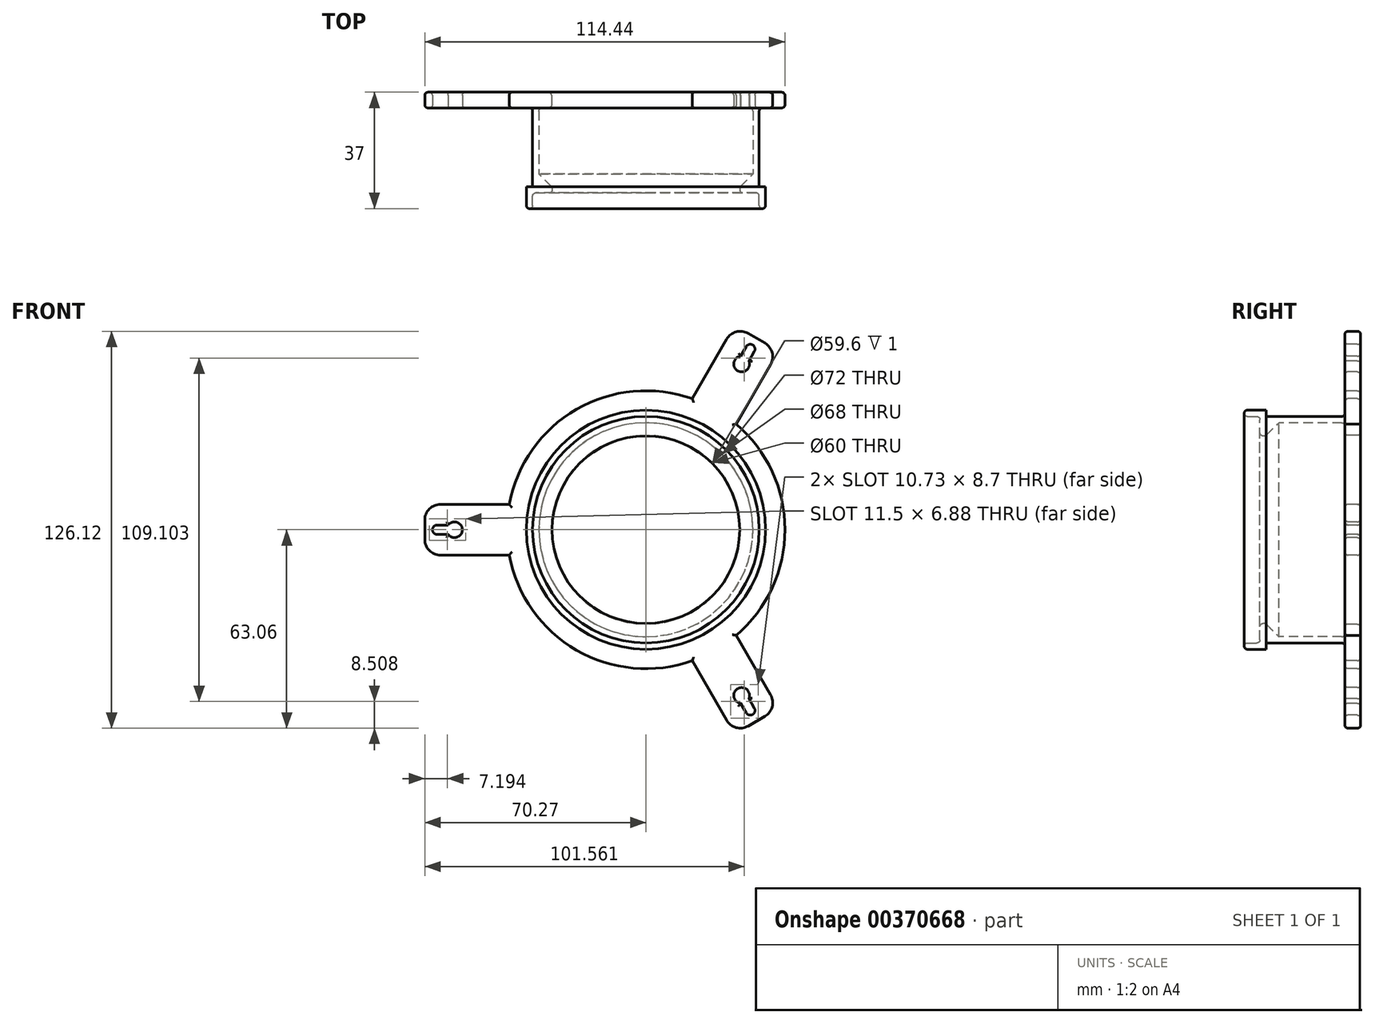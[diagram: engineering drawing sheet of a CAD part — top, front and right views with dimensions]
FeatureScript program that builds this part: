
annotation { "Feature Type Name" : "Feature", "Feature Type Description" : "" }
export const myFeature = defineFeature(function(context is Context, id is Id, definition is map)
    precondition{}
    {
        {
            var Q0;
            Q0=qCreatedBy(makeId("Front.planeOp"),FACE);
            var sketch = newSketch(context, id + "F0", { "sketchPlane" : qUnion([Q0])});
            skCircle(sketch, "E0", {"center": v(0, 0) * mm, "radius": 31.8 * mm});
            skCircle(sketch, "E1", {"center": v(0, 0) * mm, "radius": 36 * mm});
            skCircle(sketch, "E2", {"center": v(0, 0) * mm, "radius": 29.8 * mm});
            skCircle(sketch, "E3", {"center": v(0, 0) * mm, "radius": 38 * mm});
            skSolve(sketch);
        }
        {
            var Q0;
            Q0=makeQuery(id+"F0.imprint","IMPRINT",FACE,{"disambiguationData":[TD([[makeQuery(id+"F0.imprint","IMPRINT",EDGE,{"derivedFrom":sQuery(id+"F0.wireOp",EDGE,"E0")}),-1.0]])]});
            var Q1;
            Q1=makeQuery(id+"F0.imprint","IMPRINT",FACE,{"disambiguationData":[TD([[makeQuery(id+"F0.imprint","IMPRINT",EDGE,{"derivedFrom":sQuery(id+"F0.wireOp",EDGE,"E1")}),-1.0]])]});
            var Q2;
            Q2=makeQuery(id+"F0.imprint","IMPRINT",FACE,{"disambiguationData":[TD([[makeQuery(id+"F0.imprint","IMPRINT",EDGE,{"derivedFrom":sQuery(id+"F0.wireOp",EDGE,"E0")}),1.0]])]});
            extrude(context, id + "F1", {"entities" : qUnion([Q0, Q1, Q2]), "oppositeDirection" : true, "depth" : 2 * mm});
        }
        {
            var Q0;
            Q0=makeQuery(id+"F0.imprint","IMPRINT",FACE,{"disambiguationData":[TD([[makeQuery(id+"F0.imprint","IMPRINT",EDGE,{"derivedFrom":sQuery(id+"F0.wireOp",EDGE,"E1")}),-1.0]])]});
            extrude(context, id + "F2", {"entities" : qUnion([Q0]), "operationType" : NewBodyOperationType.ADD, "depth" : 5 * mm});
        }
        {
            var Q0;
            Q0=makeQuery(id+"F2.opExtrude","CAP_FACE",FACE,{"disambiguationData":[OSD([sQuery(id+"F0.wireOp",EDGE,"E1"),sQuery(id+"F0.wireOp",EDGE,"E3")])],"isStart":false});
            var Q1;
            Q1=makeQuery(id+"F2.opExtrude","CAP_FACE",FACE,{"disambiguationData":[OSD([sQuery(id+"F0.wireOp",EDGE,"E0"),sQuery(id+"F0.wireOp",EDGE,"E2")])],"isStart":false});
            var Q2;
            Q2=makeQuery(id+"F1.opExtrude","CAP_FACE",FACE,{"disambiguationData":[OSD([sQuery(id+"F0.wireOp",EDGE,"E2"),sQuery(id+"F0.wireOp",EDGE,"E3")])],"isStart":true});
            fillet(context, id + "F3", {"entities" : qUnion([Q0, Q1, Q2]), "radius" : 1 * mm, "tangentPropagation" : true, "allowEdgeOverflow" : false});
        }
        {
            var Q0;
            Q0=makeQuery(id+"F1.opExtrude","CAP_FACE",FACE,{"disambiguationData":[OSD([sQuery(id+"F0.wireOp",EDGE,"E2"),sQuery(id+"F0.wireOp",EDGE,"E3")])],"isStart":false});
            var sketch = newSketch(context, id + "F4", { "sketchPlane" : qUnion([Q0])});
            skCircle(sketch, "E4", {"center": v(0, 0) * mm, "radius": 34 * mm});
            skCircle(sketch, "E5", {"center": v(0, 0) * mm, "radius": 36 * mm});
            skSolve(sketch);
        }
        {
            var Q0;
            Q0 = qSketchRegion(id + "F4", true);
            extrude(context, id + "F5", {"entities" : qUnion([Q0]), "operationType" : NewBodyOperationType.ADD, "depth" : 25 * mm});
        }
        {
            var Q0;
            Q0=makeQuery(id+"F5.opExtrude","CAP_FACE",FACE,{"disambiguationData":[OSD([sQuery(id+"F4.wireOp",EDGE,"E4"),sQuery(id+"F4.wireOp",EDGE,"E5")])],"isStart":false});
            var sketch = newSketch(context, id + "F6", { "sketchPlane" : qUnion([Q0])});
            skCircle(sketch, "E6", {"center": v(0, 0) * mm, "radius": 30 * mm});
            skCircle(sketch, "E7", {"center": v(0, 0) * mm, "radius": 44.17 * mm});
            skLineSegment(sketch, "E8.bottom", {"start": v(35.08, 8.07) * mm, "end": v(65.27, 8.07) * mm});
            skLineSegment(sketch, "E8.top", {"start": v(35.08, -8.07) * mm, "end": v(65.27, -8.07) * mm});
            skLineSegment(sketch, "E8.left", {"start": v(35.08, 8.07) * mm, "end": v(35.08, -8.07) * mm});
            skLineSegment(sketch, "E8.right", {"start": v(70.27, 3.07) * mm, "end": v(70.27, -3.07) * mm});
            skCircle(sketch, "E9", {"center": v(60.83, 0) * mm, "radius": 2.5 * mm});
            skLineSegment(sketch, "E10.bottom", {"start": v(62.83, 1.5) * mm, "end": v(66.33, 1.5) * mm});
            skLineSegment(sketch, "E10.top", {"start": v(62.83, -1.5) * mm, "end": v(66.33, -1.5) * mm});
            skLineSegment(sketch, "E10.left", {"start": v(62.83, 1.5) * mm, "end": v(62.83, -1.5) * mm});
            skLineSegment(sketch, "E10.right", {"start": v(67.83, 0) * mm, "end": v(67.83, 0) * mm});
            skPoint(sketch, "E11.visualSharp", {"position": v(70.27, 8.07) * mm});
            skArc(sketch, "E11.filletArc", {"start": v(70.27, 3.07) * mm, "mid": v(68.8, 6.6) * mm, "end": v(65.27, 8.07) * mm});
            skPoint(sketch, "E12.visualSharp", {"position": v(70.27, -8.07) * mm});
            skArc(sketch, "E12.filletArc", {"start": v(65.27, -8.07) * mm, "mid": v(68.8, -6.6) * mm, "end": v(70.27, -3.07) * mm});
            skPoint(sketch, "E13.visualSharp", {"position": v(67.83, 1.5) * mm});
            skArc(sketch, "E13.filletArc", {"start": v(67.83, 0) * mm, "mid": v(67.39, 1.06) * mm, "end": v(66.33, 1.5) * mm});
            skPoint(sketch, "E14.visualSharp", {"position": v(67.83, -1.5) * mm});
            skArc(sketch, "E14.filletArc", {"start": v(66.33, -1.5) * mm, "mid": v(67.39, -1.06) * mm, "end": v(67.83, 0) * mm});
            skLineSegment(sketch, "E15.1.1", {"start": v(-24.53, 26.35) * mm, "end": v(-10.55, 34.42) * mm});
            skLineSegment(sketch, "E15.1.2", {"start": v(-10.55, 34.42) * mm, "end": v(-25.65, 60.56) * mm});
            skLineSegment(sketch, "E15.1.3", {"start": v(-24.53, 26.35) * mm, "end": v(-39.63, 52.5) * mm});
            skPoint(sketch, "E15.1.5", {"position": v(-42.13, 56.82) * mm});
            skPoint(sketch, "E15.1.6", {"position": v(-28.15, 64.9) * mm});
            skPoint(sketch, "E15.1.7", {"position": v(-32.61, 59.49) * mm});
            skCircle(sketch, "E15.1.8", {"center": v(-30.41, 52.68) * mm, "radius": 2.5 * mm});
            skArc(sketch, "E15.1.9", {"start": v(-37.8, 59.32) * mm, "mid": v(-40.13, 56.29) * mm, "end": v(-39.63, 52.5) * mm});
            skArc(sketch, "E15.1.10", {"start": v(-25.65, 60.56) * mm, "mid": v(-28.68, 62.9) * mm, "end": v(-32.48, 62.4) * mm});
            skPoint(sketch, "E15.1.11", {"position": v(-35.21, 57.99) * mm});
            skLineSegment(sketch, "E15.1.12", {"start": v(-37.8, 59.32) * mm, "end": v(-32.48, 62.4) * mm});
            skLineSegment(sketch, "E15.1.13", {"start": v(-32.71, 53.66) * mm, "end": v(-30.11, 55.16) * mm});
            skLineSegment(sketch, "E15.1.14", {"start": v(-32.71, 53.66) * mm, "end": v(-34.46, 56.7) * mm});
            skLineSegment(sketch, "E15.1.15", {"start": v(-30.11, 55.16) * mm, "end": v(-31.86, 58.2) * mm});
            skArc(sketch, "E15.1.16", {"start": v(-31.86, 58.2) * mm, "mid": v(-32.77, 58.89) * mm, "end": v(-33.91, 58.74) * mm});
            skArc(sketch, "E15.1.17", {"start": v(-33.91, 58.74) * mm, "mid": v(-34.61, 57.83) * mm, "end": v(-34.46, 56.7) * mm});
            skLineSegment(sketch, "E15.2.1", {"start": v(-10.55, -34.42) * mm, "end": v(-24.53, -26.35) * mm});
            skLineSegment(sketch, "E15.2.2", {"start": v(-24.53, -26.35) * mm, "end": v(-39.63, -52.5) * mm});
            skLineSegment(sketch, "E15.2.3", {"start": v(-10.55, -34.42) * mm, "end": v(-25.65, -60.56) * mm});
            skPoint(sketch, "E15.2.5", {"position": v(-28.15, -64.9) * mm});
            skPoint(sketch, "E15.2.6", {"position": v(-42.13, -56.82) * mm});
            skPoint(sketch, "E15.2.7", {"position": v(-35.21, -57.99) * mm});
            skCircle(sketch, "E15.2.8", {"center": v(-30.41, -52.68) * mm, "radius": 2.5 * mm});
            skArc(sketch, "E15.2.9", {"start": v(-32.48, -62.4) * mm, "mid": v(-28.68, -62.9) * mm, "end": v(-25.65, -60.56) * mm});
            skArc(sketch, "E15.2.10", {"start": v(-39.63, -52.5) * mm, "mid": v(-40.13, -56.29) * mm, "end": v(-37.8, -59.32) * mm});
            skPoint(sketch, "E15.2.11", {"position": v(-32.61, -59.49) * mm});
            skLineSegment(sketch, "E15.2.12", {"start": v(-32.48, -62.4) * mm, "end": v(-37.8, -59.32) * mm});
            skLineSegment(sketch, "E15.2.13", {"start": v(-30.11, -55.16) * mm, "end": v(-32.71, -53.66) * mm});
            skLineSegment(sketch, "E15.2.14", {"start": v(-30.11, -55.16) * mm, "end": v(-31.86, -58.2) * mm});
            skLineSegment(sketch, "E15.2.15", {"start": v(-32.71, -53.66) * mm, "end": v(-34.46, -56.7) * mm});
            skArc(sketch, "E15.2.16", {"start": v(-34.46, -56.7) * mm, "mid": v(-34.61, -57.83) * mm, "end": v(-33.91, -58.74) * mm});
            skArc(sketch, "E15.2.17", {"start": v(-33.91, -58.74) * mm, "mid": v(-32.77, -58.89) * mm, "end": v(-31.86, -58.2) * mm});
            skSolve(sketch);
        }
        {
            var Q0;
            Q0 = qSketchRegion(id + "F6", true);
            extrude(context, id + "F7", {"entities" : qUnion([Q0]), "operationType" : NewBodyOperationType.ADD, "depth" : 5 * mm});
        }
        {
            var Q0;
            Q0=makeQuery(id+"F5.opExtrude","CAP_EDGE",EDGE,{"disambiguationData":[OSD([sQuery(id+"F4.wireOp",EDGE,"E4")])],"isStart":true});
            var Q1;
            Q1=makeQuery(id+"F5.opExtrude","CAP_EDGE",EDGE,{"disambiguationData":[OSD([sQuery(id+"F4.wireOp",EDGE,"E5")])],"isStart":true});
            chamfer(context, id + "F8", {"entities" : qUnion([Q0, Q1]), "width" : 4 * mm, "tangentPropagation" : true});
        }
        {
            var Q0;
            Q0=makeQuery(id+"F7.opExtrude","CAP_FACE",FACE,{"disambiguationData":[OSD([sQuery(id+"F6.wireOp",EDGE,"E8.bottom"),sQuery(id+"F6.wireOp",EDGE,"E8.top"),sQuery(id+"F6.wireOp",EDGE,"E8.right"),sQuery(id+"F6.wireOp",EDGE,"E9"),sQuery(id+"F6.wireOp",EDGE,"E10.bottom"),sQuery(id+"F6.wireOp",EDGE,"E10.top"),sQuery(id+"F6.wireOp",EDGE,"E11.filletArc"),sQuery(id+"F6.wireOp",EDGE,"E12.filletArc"),sQuery(id+"F6.wireOp",EDGE,"E13.filletArc"),sQuery(id+"F6.wireOp",EDGE,"E14.filletArc"),sQuery(id+"F6.wireOp",EDGE,"E15.1.2"),sQuery(id+"F6.wireOp",EDGE,"E15.1.3"),sQuery(id+"F6.wireOp",EDGE,"E15.1.8"),sQuery(id+"F6.wireOp",EDGE,"E15.1.9"),sQuery(id+"F6.wireOp",EDGE,"E15.1.10"),sQuery(id+"F6.wireOp",EDGE,"E15.1.12"),sQuery(id+"F6.wireOp",EDGE,"E15.1.14"),sQuery(id+"F6.wireOp",EDGE,"E15.1.15"),sQuery(id+"F6.wireOp",EDGE,"E15.1.16"),sQuery(id+"F6.wireOp",EDGE,"E15.1.17"),sQuery(id+"F6.wireOp",EDGE,"E6"),sQuery(id+"F6.wireOp",EDGE,"E15.2.2"),sQuery(id+"F6.wireOp",EDGE,"E15.2.3"),sQuery(id+"F6.wireOp",EDGE,"E7"),sQuery(id+"F6.wireOp",EDGE,"E15.2.8"),sQuery(id+"F6.wireOp",EDGE,"E15.2.9"),sQuery(id+"F6.wireOp",EDGE,"E15.2.10"),sQuery(id+"F6.wireOp",EDGE,"E15.2.12"),sQuery(id+"F6.wireOp",EDGE,"E15.2.14"),sQuery(id+"F6.wireOp",EDGE,"E15.2.15"),sQuery(id+"F6.wireOp",EDGE,"E15.2.16"),sQuery(id+"F6.wireOp",EDGE,"E15.2.17")])],"isStart":true});
            var Q1;
            Q1=makeQuery(id+"F7.opExtrude","CAP_FACE",FACE,{"disambiguationData":[OSD([sQuery(id+"F6.wireOp",EDGE,"E8.bottom"),sQuery(id+"F6.wireOp",EDGE,"E8.top"),sQuery(id+"F6.wireOp",EDGE,"E8.right"),sQuery(id+"F6.wireOp",EDGE,"E9"),sQuery(id+"F6.wireOp",EDGE,"E10.bottom"),sQuery(id+"F6.wireOp",EDGE,"E10.top"),sQuery(id+"F6.wireOp",EDGE,"E11.filletArc"),sQuery(id+"F6.wireOp",EDGE,"E12.filletArc"),sQuery(id+"F6.wireOp",EDGE,"E13.filletArc"),sQuery(id+"F6.wireOp",EDGE,"E14.filletArc"),sQuery(id+"F6.wireOp",EDGE,"E15.1.2"),sQuery(id+"F6.wireOp",EDGE,"E15.1.3"),sQuery(id+"F6.wireOp",EDGE,"E15.1.8"),sQuery(id+"F6.wireOp",EDGE,"E15.1.9"),sQuery(id+"F6.wireOp",EDGE,"E15.1.10"),sQuery(id+"F6.wireOp",EDGE,"E15.1.12"),sQuery(id+"F6.wireOp",EDGE,"E15.1.14"),sQuery(id+"F6.wireOp",EDGE,"E15.1.15"),sQuery(id+"F6.wireOp",EDGE,"E15.1.16"),sQuery(id+"F6.wireOp",EDGE,"E15.1.17"),sQuery(id+"F6.wireOp",EDGE,"E6"),sQuery(id+"F6.wireOp",EDGE,"E15.2.2"),sQuery(id+"F6.wireOp",EDGE,"E15.2.3"),sQuery(id+"F6.wireOp",EDGE,"E7"),sQuery(id+"F6.wireOp",EDGE,"E15.2.8"),sQuery(id+"F6.wireOp",EDGE,"E15.2.9"),sQuery(id+"F6.wireOp",EDGE,"E15.2.10"),sQuery(id+"F6.wireOp",EDGE,"E15.2.12"),sQuery(id+"F6.wireOp",EDGE,"E15.2.14"),sQuery(id+"F6.wireOp",EDGE,"E15.2.15"),sQuery(id+"F6.wireOp",EDGE,"E15.2.16"),sQuery(id+"F6.wireOp",EDGE,"E15.2.17")])],"isStart":false});
            fillet(context, id + "F9", {"entities" : qUnion([Q0, Q1]), "radius" : 1 * mm, "tangentPropagation" : true, "allowEdgeOverflow" : false});
        }
    });
